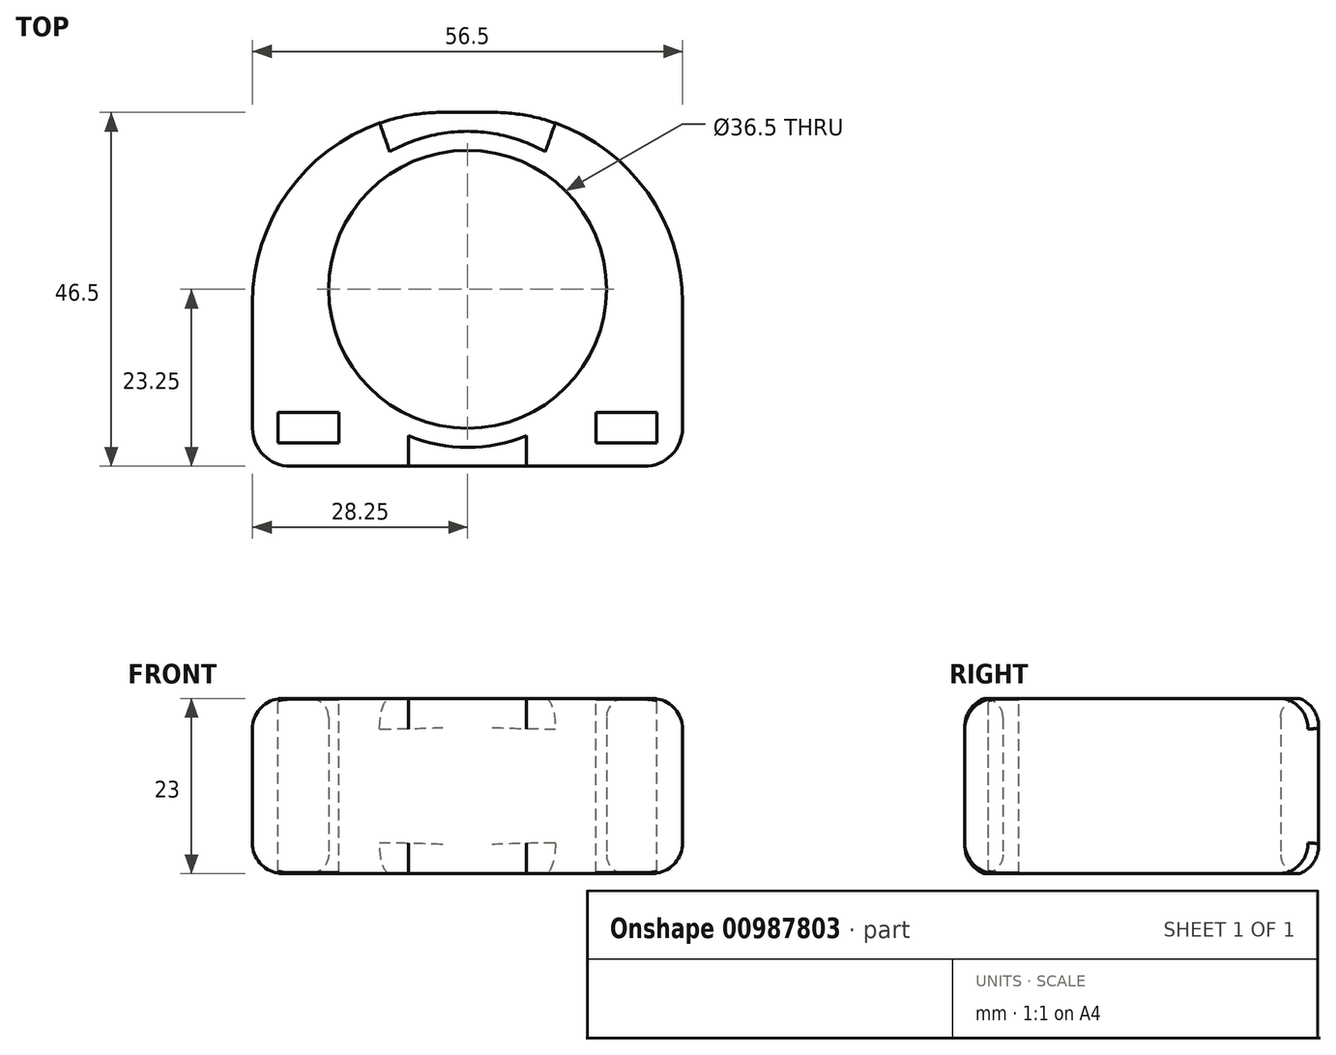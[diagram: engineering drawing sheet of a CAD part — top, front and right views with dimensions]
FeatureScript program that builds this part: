
annotation { "Feature Type Name" : "Feature", "Feature Type Description" : "" }
export const myFeature = defineFeature(function(context is Context, id is Id, definition is map)
    precondition{}
    {
        {
            var Q0;
            Q0=qCreatedBy(makeId("Top.planeOp"),FACE);
            var sketch = newSketch(context, id + "F0", { "sketchPlane" : qUnion([Q0])});
            skLineSegment(sketch, "E0.bottom", {"start": v(-28.25, 23.25) * mm, "end": v(28.25, 23.25) * mm});
            skLineSegment(sketch, "E0.top", {"start": v(-28.25, -23.25) * mm, "end": v(28.25, -23.25) * mm});
            skLineSegment(sketch, "E0.left", {"start": v(-28.25, 23.25) * mm, "end": v(-28.25, -23.25) * mm});
            skLineSegment(sketch, "E0.right", {"start": v(28.25, 23.25) * mm, "end": v(28.25, -23.25) * mm});
            skCircle(sketch, "E1", {"center": v(0, 0) * mm, "radius": 18.25 * mm});
            skLineSegment(sketch, "E2", {"start": v(-28.25, -23.25) * mm, "end": v(28.25, 23.25) * mm, "construction": true});
            skLineSegment(sketch, "E3", {"start": v(-28.25, 23.25) * mm, "end": v(28.25, -23.25) * mm, "construction": true});
            skSolve(sketch);
        }
        {
            var Q0;
            Q0 = qSketchRegion(id + "F0", true);
            extrude(context, id + "F1", {"entities" : qUnion([Q0]), "depth" : 23 * mm, "offsetDistance" : 25 * mm});
        }
        {
            var Q0;
            Q0=makeQuery(id+"F1.opExtrude","CAP_FACE",FACE,{"disambiguationData":[OSD([sQuery(id+"F0.wireOp",EDGE,"E0.bottom"),sQuery(id+"F0.wireOp",EDGE,"E0.top"),sQuery(id+"F0.wireOp",EDGE,"E0.left"),sQuery(id+"F0.wireOp",EDGE,"E0.right"),sQuery(id+"F0.wireOp",EDGE,"E1")])],"isStart":false});
            var sketch = newSketch(context, id + "F2", { "sketchPlane" : qUnion([Q0])});
            skLineSegment(sketch, "E4.bottom", {"start": v(-24.9, -16.16) * mm, "end": v(-16.9, -16.16) * mm});
            skLineSegment(sketch, "E4.top", {"start": v(-24.9, -20.16) * mm, "end": v(-16.9, -20.16) * mm});
            skLineSegment(sketch, "E4.left", {"start": v(-24.9, -16.16) * mm, "end": v(-24.9, -20.16) * mm});
            skLineSegment(sketch, "E4.right", {"start": v(-16.9, -16.16) * mm, "end": v(-16.9, -20.16) * mm});
            skLineSegment(sketch, "E5.bottom", {"start": v(16.9, -16.16) * mm, "end": v(24.9, -16.16) * mm});
            skLineSegment(sketch, "E5.top", {"start": v(16.9, -20.16) * mm, "end": v(24.9, -20.16) * mm});
            skLineSegment(sketch, "E5.left", {"start": v(16.9, -16.16) * mm, "end": v(16.9, -20.16) * mm});
            skLineSegment(sketch, "E5.right", {"start": v(24.9, -16.16) * mm, "end": v(24.9, -20.16) * mm});
            skLineSegment(sketch, "E6", {"start": v(-16.9, -20.16) * mm, "end": v(16.9, -20.16) * mm, "construction": true});
            skLineSegment(sketch, "E7", {"start": v(0, 0) * mm, "end": v(0, -23.25) * mm, "construction": true});
            skSolve(sketch);
        }
        {
            var Q0;
            Q0 = qSketchRegion(id + "F2", true);
            extrude(context, id + "F3", {"entities" : qUnion([Q0]), "operationType" : NewBodyOperationType.REMOVE, "endBound" : BoundingType.UP_TO_NEXT, "oppositeDirection" : true, "depth" : 25 * mm, "offsetDistance" : 25 * mm});
        }
        {
            var Q0;
            Q0=makeQuery(id+"F1.opExtrude","SWEPT_EDGE",EDGE,{"disambiguationData":[OSD([sQuery(id+"F0.wireOp",EDGE,"E0.top"),sQuery(id+"F0.wireOp",EDGE,"E0.right")])]});
            var Q1;
            Q1=makeQuery(id+"F1.opExtrude","SWEPT_EDGE",EDGE,{"disambiguationData":[OSD([sQuery(id+"F0.wireOp",EDGE,"E0.top"),sQuery(id+"F0.wireOp",EDGE,"E0.left")])]});
            fillet(context, id + "F4", {"entities" : qUnion([Q0, Q1]), "radius" : 5 * mm, "tangentPropagation" : true, "allowEdgeOverflow" : false});
        }
        {
            var Q0;
            Q0=makeQuery(id+"F1.opExtrude","SWEPT_EDGE",EDGE,{"disambiguationData":[OSD([sQuery(id+"F0.wireOp",EDGE,"E0.bottom"),sQuery(id+"F0.wireOp",EDGE,"E0.left")])]});
            var Q1;
            Q1=makeQuery(id+"F1.opExtrude","SWEPT_EDGE",EDGE,{"disambiguationData":[OSD([sQuery(id+"F0.wireOp",EDGE,"E0.bottom"),sQuery(id+"F0.wireOp",EDGE,"E0.right")])]});
            fillet(context, id + "F5", {"entities" : qUnion([Q0, Q1]), "radius" : 25 * mm, "tangentPropagation" : true, "allowEdgeOverflow" : false});
        }
        {
            var Q0;
            Q0=makeQuery(id+"F1.opExtrude","CAP_EDGE",EDGE,{"disambiguationData":[OSD([sQuery(id+"F0.wireOp",EDGE,"E1")])],"isStart":true});
            var Q1;
            Q1=makeQuery(id+"F1.opExtrude","CAP_EDGE",EDGE,{"disambiguationData":[OSD([sQuery(id+"F0.wireOp",EDGE,"E1")])],"isStart":false});
            fillet(context, id + "F6", {"entities" : qUnion([Q0, Q1]), "radius" : 2.5 * mm, "tangentPropagation" : true, "allowEdgeOverflow" : false});
        }
        {
            var Q0;
            Q0=makeQuery(id+"F1.opExtrude","CAP_EDGE",EDGE,{"disambiguationData":[OSD([sQuery(id+"F0.wireOp",EDGE,"E0.top")])],"isStart":false});
            var Q1;
            Q1=makeQuery(id+"F1.opExtrude","CAP_EDGE",EDGE,{"disambiguationData":[OSD([sQuery(id+"F0.wireOp",EDGE,"E0.top")])],"isStart":true});
            var Q2;
            Q2=makeQuery(id+"F1.opExtrude","CAP_EDGE",EDGE,{"disambiguationData":[OSD([sQuery(id+"F0.wireOp",EDGE,"E0.bottom")])],"isStart":true});
            var Q3;
            Q3=makeQuery(id+"F1.opExtrude","CAP_EDGE",EDGE,{"disambiguationData":[OSD([sQuery(id+"F0.wireOp",EDGE,"E0.bottom")])],"isStart":false});
            fillet(context, id + "F7", {"entities" : qUnion([Q0, Q1, Q2, Q3]), "radius" : 4 * mm, "tangentPropagation" : true, "allowEdgeOverflow" : false});
        }
    });
